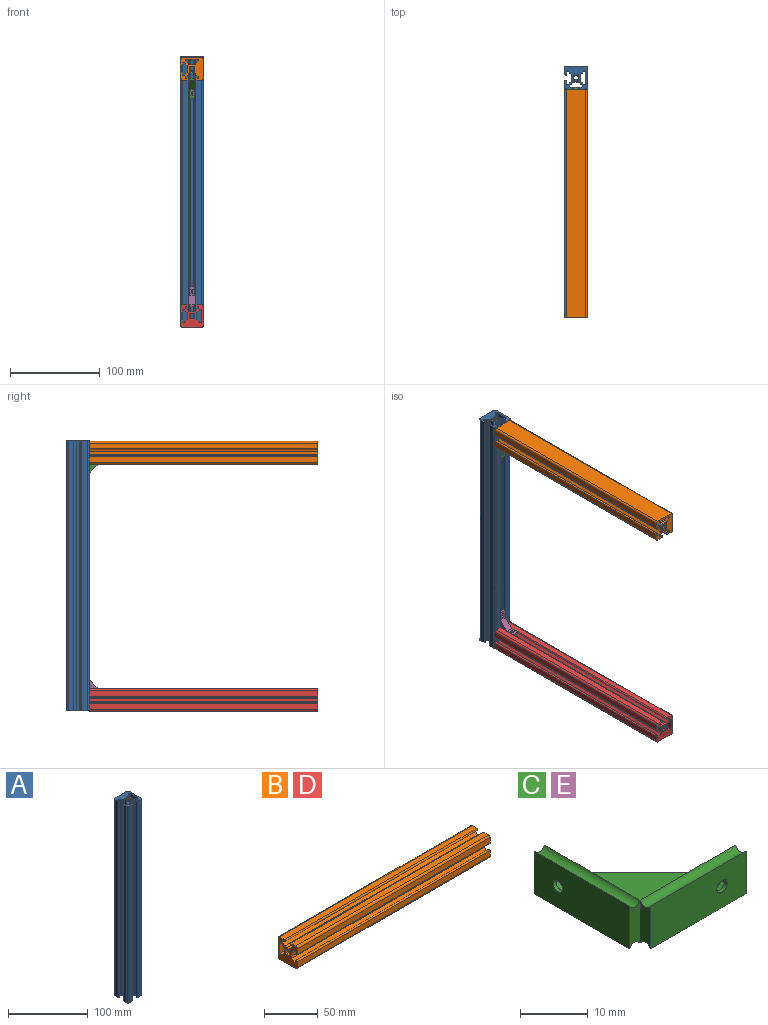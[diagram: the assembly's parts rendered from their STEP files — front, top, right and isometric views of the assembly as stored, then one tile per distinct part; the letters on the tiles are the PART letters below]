
ASSEMBLY  parts=5 mates=6
PART A: 58 faces, bbox 25.4x25.4x300.8 mm
  f0: cylinder r=3.2mm len=300.8mm, axis (0,0,1), area 749.8mm2, adj f1,f7,f24,f25
  f1: plane 300.8x3.28mm, normal (1,0,0), area 986.4mm2, adj f0,f2,f24,f25
  f2: cylinder r=3.2mm len=300.8mm, axis (0,0,1), area 749.9mm2, adj f1,f3,f24,f25
  f3: plane 300.8x3.31mm, normal (0.71,-0.71,0), area 1407.5mm2, adj f2,f4,f24,f25
  f4: cylinder r=1.02mm len=300.8mm, axis (0,0,1), area 720mm2, adj f3,f5,f24,f25
  f5: plane 300.8x12.95mm, normal (-1,0,0), area 3895.4mm2, adj f4,f6,f24,f25
  f6: cylinder r=1.02mm len=300.8mm, axis (0,0,1), area 720mm2, adj f5,f7,f24,f25
  f7: plane 300.8x3.31mm, normal (0.71,0.71,0), area 1407.6mm2, adj f0,f6,f24,f25
  f8: cylinder r=2.63mm len=300.8mm, axis (0,0,1), area 846.4mm2, adj f9,f23,f24,f25
  f9: plane 300.8x0.63mm, normal (-0.71,0.71,0), area 267.4mm2, adj f8,f10,f24,f25
  f10: cylinder r=0.63mm len=300.8mm, axis (0,0,1), area 646.7mm2, adj f9,f11,f24,f25
  f11: plane 300.8x0.63mm, normal (0.71,-0.71,0), area 267.4mm2, adj f10,f12,f24,f25
  f12: cylinder r=2.63mm len=300.8mm, axis (0,0,1), area 846.4mm2, adj f11,f13,f24,f25
  f13: plane 300.8x0.63mm, normal (0.71,0.71,0), area 267.4mm2, adj f12,f14,f24,f25
  f14: cylinder r=0.64mm len=300.8mm, axis (0,0,1), area 646.7mm2, adj f13,f15,f24,f25
  f15: plane 300.8x0.63mm, normal (-0.71,-0.71,0), area 267.4mm2, adj f14,f16,f24,f25
  f16: cylinder r=2.63mm len=300.8mm, axis (0,0,1), area 846.4mm2, adj f15,f17,f24,f25
  f17: plane 300.8x0.63mm, normal (0.71,-0.71,0), area 267.4mm2, adj f16,f18,f24,f25
  f18: cylinder r=0.64mm len=300.8mm, axis (0,0,1), area 646.7mm2, adj f17,f19,f24,f25
  f19: plane 300.8x0.63mm, normal (-0.71,0.71,0), area 267.4mm2, adj f18,f20,f24,f25
  f20: cylinder r=2.63mm len=300.8mm, axis (0,0,1), area 846.4mm2, adj f19,f21,f24,f25
  f21: plane 300.8x0.63mm, normal (-0.71,-0.71,0), area 267.4mm2, adj f20,f22,f24,f25
  f22: cylinder r=0.63mm len=300.8mm, axis (0,0,1), area 646.7mm2, adj f21,f23,f24,f25
  f23: plane 300.8x0.63mm, normal (0.71,0.71,0), area 267.4mm2, adj f8,f22,f24,f25
  f24: plane 25.4x25.4mm, normal (0,0,-1), area 378.2mm2, adj f0,f1,f2,f3,f4,f5,f6,f7
  f25: plane 25.4x25.4mm, normal (0,0,1), area 378.2mm2, adj f0,f1,f2,f3,f4,f5,f6,f7
  f26: plane 300.8x21.18mm, normal (0,1,0), area 6372.2mm2, adj f24,f25,f27,f57
  f27: cylinder r=2.11mm len=300.8mm, axis (0,0,1), area 996.1mm2, adj f24,f25,f26,f28
  f28: plane 300.8x6.24mm, normal (-1,0,0), area 1875.8mm2, adj f24,f25,f27,f29
  f29: cylinder r=1.1mm len=300.8mm, axis (0,0,1), area 1044.1mm2, adj f24,f25,f28,f30
  f30: plane 300.8x2.12mm, normal (1,0,0), area 637.4mm2, adj f24,f25,f29,f31
  f31: cylinder r=1.02mm len=300.8mm, axis (0,0,1), area 720.2mm2, adj f24,f25,f30,f32
  f32: plane 300.8x3.31mm, normal (-0.71,-0.71,0), area 1407.6mm2, adj f24,f25,f31,f33
  f33: cylinder r=3.2mm len=300.8mm, axis (0,0,1), area 749.8mm2, adj f24,f25,f32,f34
  f34: plane 300.8x3.28mm, normal (-1,0,0), area 986.4mm2, adj f24,f25,f33,f35
  f35: cylinder r=3.2mm len=300.8mm, axis (0,0,1), area 749.9mm2, adj f24,f25,f34,f36
  f36: plane 300.8x3.31mm, normal (-0.71,0.71,0), area 1407.5mm2, adj f24,f25,f35,f37
  f37: cylinder r=1.02mm len=300.8mm, axis (0,0,1), area 720.2mm2, adj f24,f25,f36,f38
  f38: plane 300.8x2.12mm, normal (1,0,0), area 637.4mm2, adj f24,f25,f37,f39
  f39: cylinder r=1.1mm len=300.8mm, axis (0,0,1), area 1044.1mm2, adj f24,f25,f38,f40
  f40: plane 300.8x6.24mm, normal (-1,0,0), area 1875.6mm2, adj f24,f25,f39,f41
  f41: cylinder r=2.11mm len=300.8mm, axis (0,0,1), area 996.1mm2, adj f24,f25,f40,f42
  f42: plane 300.8x6.24mm, normal (0,-1,0), area 1875.8mm2, adj f24,f25,f41,f43
  f43: cylinder r=1.1mm len=300.8mm, axis (0,0,1), area 1044.1mm2, adj f24,f25,f42,f44
  f44: plane 300.8x2.12mm, normal (0,1,0), area 637.2mm2, adj f24,f25,f43,f45
  f45: cylinder r=1.02mm len=300.8mm, axis (0,0,1), area 720.2mm2, adj f24,f25,f44,f46
  f46: plane 300.8x3.31mm, normal (0.71,-0.71,0), area 1407.3mm2, adj f24,f25,f45,f47
  f47: cylinder r=3.2mm len=300.8mm, axis (0,0,1), area 749.9mm2, adj f24,f25,f46,f48
  f48: plane 300.8x3.28mm, normal (0,-1,0), area 986.4mm2, adj f24,f25,f47,f49
  f49: cylinder r=3.2mm len=300.8mm, axis (0,0,1), area 749.9mm2, adj f24,f25,f48,f50
  f50: plane 300.8x3.31mm, normal (-0.71,-0.71,0), area 1407.4mm2, adj f24,f25,f49,f51
  f51: cylinder r=1.02mm len=300.8mm, axis (0,0,1), area 720mm2, adj f24,f25,f50,f52
  f52: plane 300.8x2.12mm, normal (0,1,0), area 637.3mm2, adj f24,f25,f51,f53
  f53: cylinder r=1.1mm len=300.8mm, axis (0,0,1), area 1044.1mm2, adj f24,f25,f52,f54
  f54: plane 300.8x6.24mm, normal (0,-1,0), area 1875.8mm2, adj f24,f25,f53,f55
  f55: cylinder r=2.11mm len=300.8mm, axis (0,0,1), area 996.1mm2, adj f24,f25,f54,f56
  f56: plane 300.8x21.18mm, normal (1,0,0), area 6372mm2, adj f24,f25,f55,f57
  f57: cylinder r=2.11mm len=300.8mm, axis (0,0,1), area 996.1mm2, adj f24,f25,f26,f56
PART B: 58 faces, bbox 254x25.4x25.4 mm
  f0: cylinder r=1.02mm len=254mm, axis (1,0,0), area 608mm2, adj f1,f7,f24,f25
  f1: plane 254x3.31mm, normal (0,0.71,0.71), area 1188.5mm2, adj f0,f2,f24,f25
  f2: cylinder r=3.2mm len=254mm, axis (1,0,0), area 633.2mm2, adj f1,f3,f24,f25
  f3: plane 254x3.28mm, normal (0,1,0), area 832.9mm2, adj f2,f4,f24,f25
  f4: cylinder r=3.2mm len=254mm, axis (1,0,0), area 633.2mm2, adj f3,f5,f24,f25
  f5: plane 254x3.31mm, normal (0,0.71,-0.71), area 1188.6mm2, adj f4,f6,f24,f25
  f6: cylinder r=1.02mm len=254mm, axis (1,0,0), area 608mm2, adj f5,f7,f24,f25
  f7: plane 254x12.95mm, normal (0,-1,0), area 3289.3mm2, adj f0,f6,f24,f25
  f8: cylinder r=2.63mm len=254mm, axis (1,0,0), area 714.8mm2, adj f9,f23,f24,f25
  f9: plane 254x0.63mm, normal (0,-0.71,-0.71), area 225.8mm2, adj f8,f10,f24,f25
  f10: cylinder r=0.64mm len=254mm, axis (1,0,0), area 546mm2, adj f9,f11,f24,f25
  f11: plane 254x0.63mm, normal (0,0.71,0.71), area 225.8mm2, adj f10,f12,f24,f25
  f12: cylinder r=2.63mm len=254mm, axis (1,0,0), area 714.8mm2, adj f11,f13,f24,f25
  f13: plane 254x0.63mm, normal (0,-0.71,0.71), area 225.8mm2, adj f12,f14,f24,f25
  f14: cylinder r=0.64mm len=254mm, axis (1,0,0), area 546mm2, adj f13,f15,f24,f25
  f15: plane 254x0.63mm, normal (0,0.71,-0.71), area 225.8mm2, adj f14,f16,f24,f25
  f16: cylinder r=2.63mm len=254mm, axis (1,0,0), area 714.8mm2, adj f15,f17,f24,f25
  f17: plane 254x0.63mm, normal (0,0.71,0.71), area 225.8mm2, adj f16,f18,f24,f25
  f18: cylinder r=0.63mm len=254mm, axis (1,0,0), area 546.1mm2, adj f17,f19,f24,f25
  f19: plane 254x0.63mm, normal (0,-0.71,-0.71), area 225.8mm2, adj f18,f20,f24,f25
  f20: cylinder r=2.63mm len=254mm, axis (1,0,0), area 714.8mm2, adj f19,f21,f24,f25
  f21: plane 254x0.63mm, normal (0,0.71,-0.71), area 225.8mm2, adj f20,f22,f24,f25
  f22: cylinder r=0.63mm len=254mm, axis (1,0,0), area 546.1mm2, adj f21,f23,f24,f25
  f23: plane 254x0.63mm, normal (0,-0.71,0.71), area 225.8mm2, adj f8,f22,f24,f25
  f24: plane 25.4x25.4mm, normal (-1,0,0), area 378.2mm2, adj f0,f1,f2,f3,f4,f5,f6,f7
  f25: plane 25.4x25.4mm, normal (1,0,0), area 378.2mm2, adj f0,f1,f2,f3,f4,f5,f6,f7
  f26: plane 254x6.24mm, normal (0,0,1), area 1583.9mm2, adj f24,f25,f27,f57
  f27: cylinder r=1.1mm len=254mm, axis (1,0,0), area 881.7mm2, adj f24,f25,f26,f28
  f28: plane 254x2.12mm, normal (0,0,-1), area 538.1mm2, adj f24,f25,f27,f29
  f29: cylinder r=1.02mm len=254mm, axis (1,0,0), area 608mm2, adj f24,f25,f28,f30
  f30: plane 254x3.31mm, normal (0,-0.71,0.71), area 1188.4mm2, adj f24,f25,f29,f31
  f31: cylinder r=3.2mm len=254mm, axis (1,0,0), area 633.2mm2, adj f24,f25,f30,f32
  f32: plane 254x3.28mm, normal (0,0,1), area 832.9mm2, adj f24,f25,f31,f33
  f33: cylinder r=3.2mm len=254mm, axis (1,0,0), area 633.2mm2, adj f24,f25,f32,f34
  f34: plane 254x3.31mm, normal (0,0.71,0.71), area 1188.3mm2, adj f24,f25,f33,f35
  f35: cylinder r=1.02mm len=254mm, axis (1,0,0), area 608.1mm2, adj f24,f25,f34,f36
  f36: plane 254x2.12mm, normal (0,0,-1), area 538.1mm2, adj f24,f25,f35,f37
  f37: cylinder r=1.1mm len=254mm, axis (1,0,0), area 881.7mm2, adj f24,f25,f36,f38
  f38: plane 254x6.24mm, normal (0,0,1), area 1583.9mm2, adj f24,f25,f37,f39
  f39: cylinder r=2.11mm len=254mm, axis (1,0,0), area 841.1mm2, adj f24,f25,f38,f40
  f40: plane 254x6.24mm, normal (0,-1,0), area 1583.8mm2, adj f24,f25,f39,f41
  f41: cylinder r=1.1mm len=254mm, axis (1,0,0), area 881.7mm2, adj f24,f25,f40,f42
  f42: plane 254x2.12mm, normal (0,1,0), area 538.2mm2, adj f24,f25,f41,f43
  f43: cylinder r=1.02mm len=254mm, axis (1,0,0), area 608.1mm2, adj f24,f25,f42,f44
  f44: plane 254x3.31mm, normal (0,-0.71,-0.71), area 1188.5mm2, adj f24,f25,f43,f45
  f45: cylinder r=3.2mm len=254mm, axis (1,0,0), area 633.2mm2, adj f24,f25,f44,f46
  f46: plane 254x3.28mm, normal (0,-1,0), area 832.9mm2, adj f24,f25,f45,f47
  f47: cylinder r=3.2mm len=254mm, axis (1,0,0), area 633.2mm2, adj f24,f25,f46,f48
  f48: plane 254x3.31mm, normal (0,-0.71,0.71), area 1188.6mm2, adj f24,f25,f47,f49
  f49: cylinder r=1.02mm len=254mm, axis (1,0,0), area 608.1mm2, adj f24,f25,f48,f50
  f50: plane 254x2.12mm, normal (0,1,0), area 538.2mm2, adj f24,f25,f49,f51
  f51: cylinder r=1.1mm len=254mm, axis (1,0,0), area 881.7mm2, adj f24,f25,f50,f52
  f52: plane 254x6.24mm, normal (0,-1,0), area 1583.9mm2, adj f24,f25,f51,f53
  f53: cylinder r=2.11mm len=254mm, axis (1,0,0), area 841.1mm2, adj f24,f25,f52,f54
  f54: plane 254x21.18mm, normal (0,0,-1), area 5380.8mm2, adj f24,f25,f53,f55
  f55: cylinder r=2.11mm len=254mm, axis (1,0,0), area 841.1mm2, adj f24,f25,f54,f56
  f56: plane 254x21.18mm, normal (0,1,0), area 5380.6mm2, adj f24,f25,f55,f57
  f57: cylinder r=2.11mm len=254mm, axis (1,0,0), area 841.1mm2, adj f24,f25,f26,f56
PART C: 31 faces, bbox 22.2x22.2x7.8 mm
  f0: plane 10x7.75mm, normal (1,0,0), area 62.2mm2, adj f5,f6,f7,f15,f23,f24,f25,f26
  f1: plane 10x7.75mm, normal (0,1,0), area 62.2mm2, adj f3,f10,f12,f15,f16,f17,f18,f19
  f2: cylinder r=1.1mm len=2.2mm, axis (0,1,0), area 4.2mm2, adj f11,f22
  f3: plane 7.75x2.21mm, normal (1,0,0), area 14.8mm2, adj f1,f10,f11,f12
  f4: plane 7.75x2.21mm, normal (0,-1,0), area 14.8mm2, adj f6,f7,f8,f9
  f5: plane 7.75x2.21mm, normal (0,1,0), area 14.8mm2, adj f0,f6,f7,f8
  f6: cylinder r=1.2mm len=20mm, axis (0,1,0), area 55.9mm2, adj f0,f4,f5,f8,f14
  f7: cylinder r=1.2mm len=20mm, axis (0,1,0), area 55.9mm2, adj f0,f4,f5,f8,f13
  f8: plane 20x7.75mm, normal (-1,0,0), area 151.9mm2, adj f4,f5,f6,f7,f30
  f9: plane 7.75x2.21mm, normal (-1,0,0), area 14.8mm2, adj f4,f10,f11,f12
  f10: cylinder r=1.2mm len=20mm, axis (1,0,0), area 55.9mm2, adj f1,f3,f9,f11,f14
  f11: plane 20x7.75mm, normal (0,-1,0), area 151.2mm2, adj f2,f3,f9,f10,f12
  f12: cylinder r=1.2mm len=20mm, axis (1,0,0), area 55.9mm2, adj f1,f3,f9,f11,f13
  f13: plane 10x10mm, normal (0,0,-1), area 50mm2, adj f7,f12,f15
  f14: plane 10x10mm, normal (0,0,1), area 50mm2, adj f6,f10,f15
  f15: plane 10x10mm, normal (0.71,0.71,0), area 109.6mm2, adj f0,f1,f13,f14
  f16: plane 2.43x1.6mm, normal (1,0,0), area 3.9mm2, adj f1,f17,f21,f22
  f17: plane 2.1x1.6mm, normal (0.5,0,-0.87), area 3.9mm2, adj f1,f16,f18,f22
  f18: plane 2.1x1.6mm, normal (-0.5,0,-0.87), area 3.9mm2, adj f1,f17,f19,f22
  f19: plane 2.43x1.6mm, normal (-1,0,0), area 3.9mm2, adj f1,f18,f20,f22
  f20: plane 2.1x1.6mm, normal (-0.5,0,0.87), area 3.9mm2, adj f1,f19,f21,f22
  f21: plane 2.1x1.6mm, normal (0.5,0,0.87), area 3.9mm2, adj f1,f16,f20,f22
  f22: plane 4.85x4.2mm, normal (0,1,0), area 11.5mm2, adj f2,f16,f17,f18,f19,f20,f21
  f23: plane 2.43x1.6mm, normal (0,-1,0), area 3.9mm2, adj f0,f24,f28,f29
  f24: plane 2.1x1.6mm, normal (0,-0.5,-0.87), area 3.9mm2, adj f0,f23,f25,f29
  f25: plane 2.1x1.6mm, normal (0,0.5,-0.87), area 3.9mm2, adj f0,f24,f26,f29
  f26: plane 2.43x1.6mm, normal (0,1,0), area 3.9mm2, adj f0,f25,f27,f29
  f27: plane 2.1x1.6mm, normal (0,0.5,0.87), area 3.9mm2, adj f0,f26,f28,f29
  f28: plane 2.1x1.6mm, normal (0,-0.5,0.87), area 3.9mm2, adj f0,f23,f27,f29
  f29: plane 4.85x4.2mm, normal (1,0,0), area 12.1mm2, adj f23,f24,f25,f26,f27,f28,f30
  f30: cylinder r=1mm len=2mm, axis (1,0,0), area 3.8mm2, adj f8,f29
PART D: same geometry as B
PART E: same geometry as C
PLACE A rot(axis=(0,1,0),0deg) t=(-139.7,-139.7,12.7)mm
PLACE B rot(axis=(0.58,-0.58,-0.58),120deg) t=(0,-139.7,147.47)mm
PLACE C rot(axis=(-0.58,0.58,-0.58),120deg) t=(0,0,287.17)mm
PLACE D rot(axis=(0,0,-1),90deg) t=(-139.7,-139.7,12.19)mm
PLACE E rot(axis=(-0.71,0,-0.71),180deg) t=(0,0,12.19)mm
MATE slider C.f10 <-> B.f51  axis (0,-1,0) through (4.36,-12.7,275.58)mm
MATE slider D.f27 <-> E.f6  axis (0,1,0) through (4.36,-12.7,23.79)mm
MATE slider C.f7 <-> A.f43  axis (0,0,1) through (-4.36,-11.59,274.47)mm
MATE parallel D.f57 <-> A.f54  axis (0,1,0) through (10.59,-12.7,22.78)mm
MATE slider E.f12 <-> A.f43  axis (0,0,-1) through (-4.36,-11.59,24.89)mm
MATE parallel B.f57 <-> A.f54  axis (0,1,0) through (-10.59,-12.7,297.77)mm
